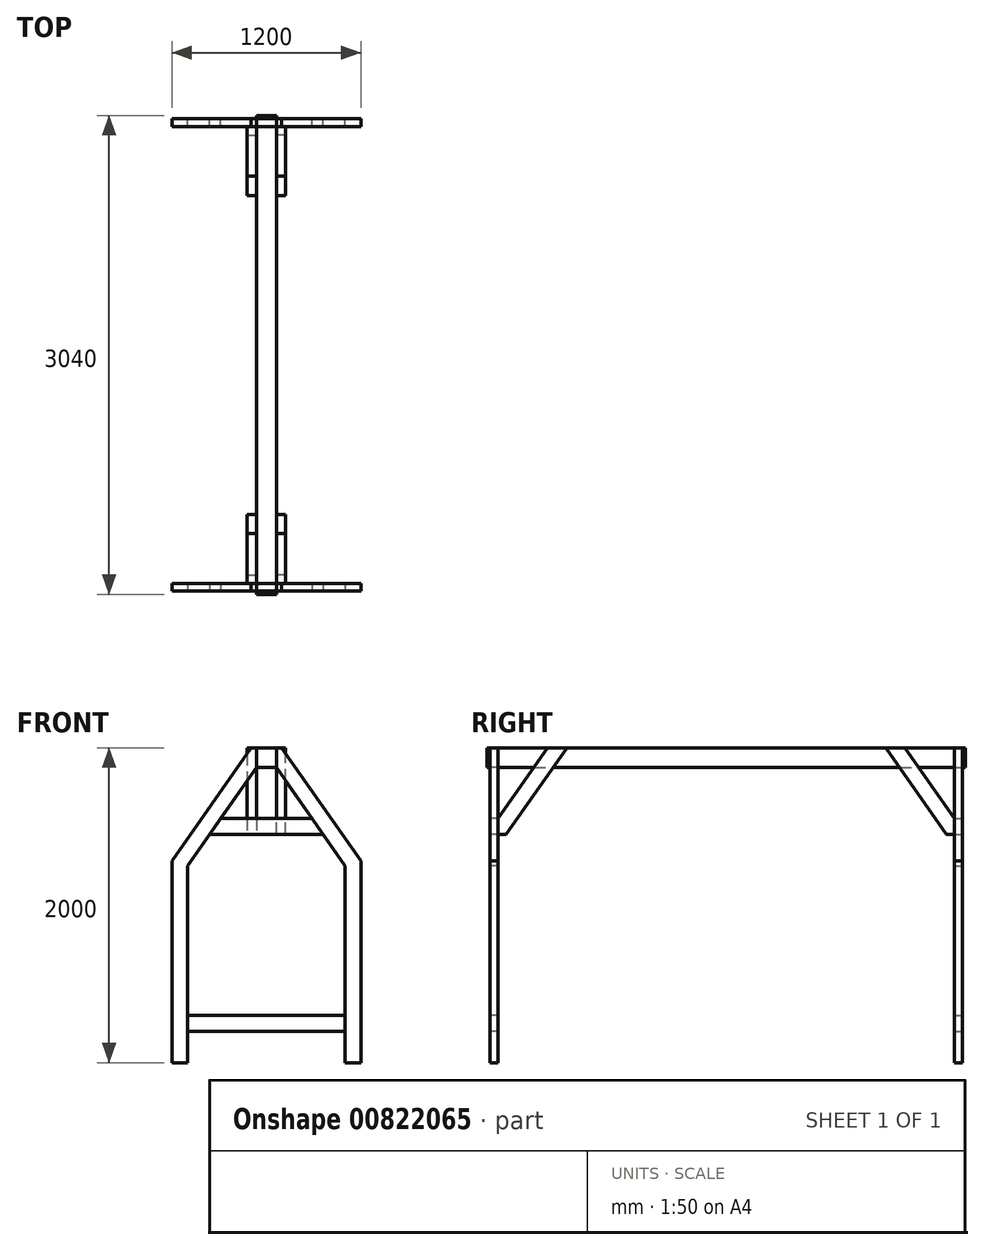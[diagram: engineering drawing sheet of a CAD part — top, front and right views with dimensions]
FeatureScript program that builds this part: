
annotation { "Feature Type Name" : "Feature", "Feature Type Description" : "" }
export const myFeature = defineFeature(function(context is Context, id is Id, definition is map)
    precondition{}
    {
        {
            var Q0;
            Q0=qCreatedBy(makeId("Front.planeOp"),FACE);
            var sketch = newSketch(context, id + "F0", { "sketchPlane" : qUnion([Q0])});
            skLineSegment(sketch, "E0", {"start": v(-97.05, 2000) * mm, "end": v(0, 2000) * mm});
            skLineSegment(sketch, "E1", {"start": v(-97.05, 2000) * mm, "end": v(-600, 1281.72) * mm});
            skLineSegment(sketch, "E2", {"start": v(-600, 1281.72) * mm, "end": v(-600, 0) * mm});
            skLineSegment(sketch, "E3", {"start": v(0, 2000) * mm, "end": v(0, 0) * mm, "construction": true});
            skLineSegment(sketch, "E4.MirrorCS", {"start": v(600, 1281.72) * mm, "end": v(600, 0) * mm});
            skLineSegment(sketch, "E5.MirrorCS", {"start": v(97.05, 2000) * mm, "end": v(0, 2000) * mm});
            skLineSegment(sketch, "E6.MirrorCS", {"start": v(97.05, 2000) * mm, "end": v(600, 1281.72) * mm});
            skLineSegment(sketch, "E7", {"start": v(0, 1875) * mm, "end": v(-62.5, 1875) * mm});
            skLineSegment(sketch, "E8", {"start": v(-62.5, 1875) * mm, "end": v(-500, 1250.19) * mm});
            skLineSegment(sketch, "E9", {"start": v(-500, 1250.19) * mm, "end": v(-500, 0) * mm});
            skLineSegment(sketch, "E10", {"start": v(-500, 0) * mm, "end": v(-600, 0) * mm});
            skLineSegment(sketch, "E11", {"start": v(-581.92, 1307.54) * mm, "end": v(-500, 1250.19) * mm, "construction": true});
            skLineSegment(sketch, "E12.MirrorCS", {"start": v(500, 0) * mm, "end": v(600, 0) * mm});
            skLineSegment(sketch, "E13.MirrorCS", {"start": v(500, 1250.19) * mm, "end": v(500, 0) * mm});
            skLineSegment(sketch, "E14.MirrorCS", {"start": v(0, 1875) * mm, "end": v(62.5, 1875) * mm});
            skLineSegment(sketch, "E15.MirrorCS", {"start": v(62.5, 1875) * mm, "end": v(500, 1250.19) * mm});
            skLineSegment(sketch, "E16", {"start": v(-62.5, 1875) * mm, "end": v(-62.5, 2000) * mm, "construction": true});
            skLineSegment(sketch, "E17", {"start": v(500, 1250.19) * mm, "end": v(600, 1281.72) * mm, "construction": true});
            skSolve(sketch);
        }
        {
            var Q0;
            Q0=makeQuery(id+"F0.imprint","IMPRINT",FACE,{"disambiguationData":[TD([[makeQuery(id+"F0.imprint","IMPRINT",EDGE,{"derivedFrom":sQuery(id+"F0.wireOp",EDGE,"E0")}),-1.0]])]});
            extrude(context, id + "F1", {"entities" : qUnion([Q0]), "depth" : 50 * mm, "offsetDistance" : 25 * mm});
        }
        {
            var Q0;
            Q0=qCreatedBy(makeId("Front.planeOp"),FACE);
            cPlane(context, id + "F2", {"entities" : qUnion([Q0]), "cplaneType" : CPlaneType.OFFSET, "offset" : 3000 * mm, "width" : 150 * mm, "height" : 150 * mm});
        }
        {
            var Q0;
            Q0=qCreatedBy(id+"F2.planeOp",FACE);
            var sketch = newSketch(context, id + "F3", { "sketchPlane" : qUnion([Q0])});
            skLineSegment(sketch, "E18.0.0", {"start": v(-62.5, 1875) * mm, "end": v(62.5, 1875) * mm});
            skLineSegment(sketch, "E18.0.1", {"start": v(62.5, 1875) * mm, "end": v(500, 1250.19) * mm});
            skLineSegment(sketch, "E18.0.2", {"start": v(500, 1250.19) * mm, "end": v(500, 0) * mm});
            skLineSegment(sketch, "E18.0.3", {"start": v(500, 0) * mm, "end": v(600, 0) * mm});
            skLineSegment(sketch, "E18.0.4", {"start": v(600, 0) * mm, "end": v(600, 1281.72) * mm});
            skLineSegment(sketch, "E18.0.5", {"start": v(600, 1281.72) * mm, "end": v(97.05, 2000) * mm});
            skLineSegment(sketch, "E18.0.6", {"start": v(97.05, 2000) * mm, "end": v(-97.05, 2000) * mm});
            skLineSegment(sketch, "E18.0.7", {"start": v(-97.05, 2000) * mm, "end": v(-600, 1281.72) * mm});
            skLineSegment(sketch, "E18.0.8", {"start": v(-600, 1281.72) * mm, "end": v(-600, 0) * mm});
            skLineSegment(sketch, "E18.0.9", {"start": v(-600, 0) * mm, "end": v(-500, 0) * mm});
            skLineSegment(sketch, "E18.0.10", {"start": v(-500, 0) * mm, "end": v(-500, 1250.19) * mm});
            skLineSegment(sketch, "E18.0.11", {"start": v(-500, 1250.19) * mm, "end": v(-62.5, 1875) * mm});
            skSolve(sketch);
        }
        {
            var Q0;
            Q0=makeQuery(id+"F3.imprint","IMPRINT",FACE,{"disambiguationData":[TD([[makeQuery(id+"F3.imprint","IMPRINT",EDGE,{"derivedFrom":sQuery(id+"F3.wireOp",EDGE,"E18.0.0")}),1.0]])]});
            extrude(context, id + "F4", {"entities" : qUnion([Q0]), "oppositeDirection" : true, "depth" : 50 * mm, "offsetDistance" : 25 * mm});
        }
        {
            var Q0;
            Q0=qCreatedBy(makeId("Front.planeOp"),FACE);
            var sketch = newSketch(context, id + "F5", { "sketchPlane" : qUnion([Q0])});
            skLineSegment(sketch, "E19.bottom", {"start": v(-62.5, 2000) * mm, "end": v(62.5, 2000) * mm});
            skLineSegment(sketch, "E19.top", {"start": v(-62.5, 1875) * mm, "end": v(62.5, 1875) * mm});
            skLineSegment(sketch, "E19.left", {"start": v(-62.5, 2000) * mm, "end": v(-62.5, 1875) * mm});
            skLineSegment(sketch, "E19.right", {"start": v(62.5, 2000) * mm, "end": v(62.5, 1875) * mm});
            skLineSegment(sketch, "E20", {"start": v(0, 1875) * mm, "end": v(0, 2019) * mm, "construction": true});
            skPoint(sketch, "E20.startSnap0", {"position": v(-18.36, 1875) * mm});
            skSolve(sketch);
        }
        {
            var Q0;
            Q0=qSketchRegion(id+"F5",true);
            extrude(context, id + "F6", {"entities" : qUnion([Q0]), "depth" : 3020 * mm, "offsetDistance" : 25 * mm, "hasSecondDirection" : true, "secondDirectionOppositeDirection" : true, "secondDirectionDepth" : 20 * mm});
        }
        {
            var Q0;
            Q0=qCreatedBy(id+"F2.planeOp",FACE);
            var sketch = newSketch(context, id + "F7", { "sketchPlane" : qUnion([Q0])});
            skLineSegment(sketch, "E21.bottom", {"start": v(-360.09, 1450) * mm, "end": v(360.09, 1450) * mm});
            skLineSegment(sketch, "E21.top", {"start": v(-290.07, 1550) * mm, "end": v(290.07, 1550) * mm});
            skLineSegment(sketch, "E22.bottom", {"start": v(-500, 300) * mm, "end": v(500, 300) * mm});
            skLineSegment(sketch, "E22.top", {"start": v(-500, 200) * mm, "end": v(500, 200) * mm});
            skLineSegment(sketch, "E22.left", {"start": v(-500, 300) * mm, "end": v(-500, 200) * mm});
            skLineSegment(sketch, "E22.right", {"start": v(500, 300) * mm, "end": v(500, 200) * mm});
            skLineSegment(sketch, "E23", {"start": v(-360.09, 1450) * mm, "end": v(-290.07, 1550) * mm});
            skLineSegment(sketch, "E24", {"start": v(360.09, 1450) * mm, "end": v(290.07, 1550) * mm});
            skSolve(sketch);
        }
        {
            var Q0;
            Q0=qSketchRegion(id+"F7",true);
            extrude(context, id + "F8", {"entities" : qUnion([Q0]), "oppositeDirection" : true, "depth" : 50 * mm, "offsetDistance" : 25 * mm});
        }
        {
            var Q0;
            Q0=qCreatedBy(makeId("Front.planeOp"),FACE);
            var sketch = newSketch(context, id + "F9", { "sketchPlane" : qUnion([Q0])});
            skLineSegment(sketch, "E25.0.0", {"start": v(-500, 300) * mm, "end": v(-500, 200) * mm});
            skLineSegment(sketch, "E25.0.1", {"start": v(-500, 200) * mm, "end": v(500, 200) * mm});
            skLineSegment(sketch, "E25.0.2", {"start": v(500, 200) * mm, "end": v(500, 300) * mm});
            skLineSegment(sketch, "E25.0.3", {"start": v(500, 300) * mm, "end": v(-500, 300) * mm});
            skLineSegment(sketch, "E26.0.0", {"start": v(290.07, 1550) * mm, "end": v(-290.07, 1550) * mm});
            skLineSegment(sketch, "E26.0.1", {"start": v(-290.07, 1550) * mm, "end": v(-360.09, 1450) * mm});
            skLineSegment(sketch, "E26.0.2", {"start": v(-360.09, 1450) * mm, "end": v(360.09, 1450) * mm});
            skLineSegment(sketch, "E26.0.3", {"start": v(360.09, 1450) * mm, "end": v(290.07, 1550) * mm});
            skSolve(sketch);
        }
        {
            var Q0;
            Q0=qSketchRegion(id+"F9",true);
            extrude(context, id + "F10", {"entities" : qUnion([Q0]), "depth" : 50 * mm, "offsetDistance" : 25 * mm});
        }
        {
            var Q0;
            Q0=makeQuery(id+"F6.opExtrude","SWEPT_FACE",FACE,{"disambiguationData":[OSD([sQuery(id+"F5.wireOp",EDGE,"E19.right")])]});
            var sketch = newSketch(context, id + "F11", { "sketchPlane" : qUnion([Q0])});
            skLineSegment(sketch, "E27", {"start": v(-2950, 1550) * mm, "end": v(-2634.9, 2000) * mm});
            skLineSegment(sketch, "E28", {"start": v(-2634.9, 2000) * mm, "end": v(-2512.83, 2000) * mm});
            skLineSegment(sketch, "E29", {"start": v(-2512.83, 2000) * mm, "end": v(-2897.94, 1450) * mm});
            skLineSegment(sketch, "E30", {"start": v(-2950, 1450) * mm, "end": v(-2950, 1550) * mm});
            skLineSegment(sketch, "E31", {"start": v(-1500, 1875) * mm, "end": v(-1500, 1158.19) * mm, "construction": true});
            skLineSegment(sketch, "E32", {"start": v(-2142.12, 1550) * mm, "end": v(-1961.4, 1550) * mm, "construction": true});
            skLineSegment(sketch, "E33", {"start": v(-2950, 1450) * mm, "end": v(-2897.94, 1450) * mm});
            skLineSegment(sketch, "E34.MirrorCS", {"start": v(-365.1, 2000) * mm, "end": v(-487.17, 2000) * mm});
            skLineSegment(sketch, "E35.MirrorCS", {"start": v(-487.17, 2000) * mm, "end": v(-102.06, 1450) * mm});
            skLineSegment(sketch, "E36.MirrorCS", {"start": v(-50, 1550) * mm, "end": v(-365.1, 2000) * mm});
            skLineSegment(sketch, "E37.MirrorCS", {"start": v(-50, 1450) * mm, "end": v(-50, 1550) * mm});
            skLineSegment(sketch, "E38.MirrorCS", {"start": v(-50, 1450) * mm, "end": v(-102.06, 1450) * mm});
            skSolve(sketch);
        }
        {
            var Q0;
            Q0=qSketchRegion(id+"F11",true);
            extrude(context, id + "F12", {"entities" : qUnion([Q0]), "depth" : 60 * mm, "offsetDistance" : 25 * mm});
        }
        {
            var Q0;
            Q0=makeQuery(id+"F6.opExtrude","SWEPT_FACE",FACE,{"disambiguationData":[OSD([sQuery(id+"F5.wireOp",EDGE,"E19.left")])]});
            var sketch = newSketch(context, id + "F13", { "sketchPlane" : qUnion([Q0])});
            skLineSegment(sketch, "E39.0.0", {"start": v(50, 1450) * mm, "end": v(50, 1550) * mm});
            skLineSegment(sketch, "E39.0.1", {"start": v(50, 1550) * mm, "end": v(365.1, 2000) * mm});
            skLineSegment(sketch, "E39.0.2", {"start": v(365.1, 2000) * mm, "end": v(487.17, 2000) * mm});
            skLineSegment(sketch, "E39.0.3", {"start": v(487.17, 2000) * mm, "end": v(102.06, 1450) * mm});
            skLineSegment(sketch, "E39.0.4", {"start": v(102.06, 1450) * mm, "end": v(50, 1450) * mm});
            skLineSegment(sketch, "E40.0.0", {"start": v(2897.94, 1450) * mm, "end": v(2512.83, 2000) * mm});
            skLineSegment(sketch, "E40.0.1", {"start": v(2512.83, 2000) * mm, "end": v(2634.9, 2000) * mm});
            skLineSegment(sketch, "E40.0.2", {"start": v(2634.9, 2000) * mm, "end": v(2950, 1550) * mm});
            skLineSegment(sketch, "E40.0.3", {"start": v(2950, 1550) * mm, "end": v(2950, 1450) * mm});
            skLineSegment(sketch, "E40.0.4", {"start": v(2950, 1450) * mm, "end": v(2897.94, 1450) * mm});
            skSolve(sketch);
        }
        {
            var Q0;
            Q0=qSketchRegion(id+"F13",true);
            extrude(context, id + "F14", {"entities" : qUnion([Q0]), "depth" : 60 * mm, "offsetDistance" : 25 * mm});
        }
    });
